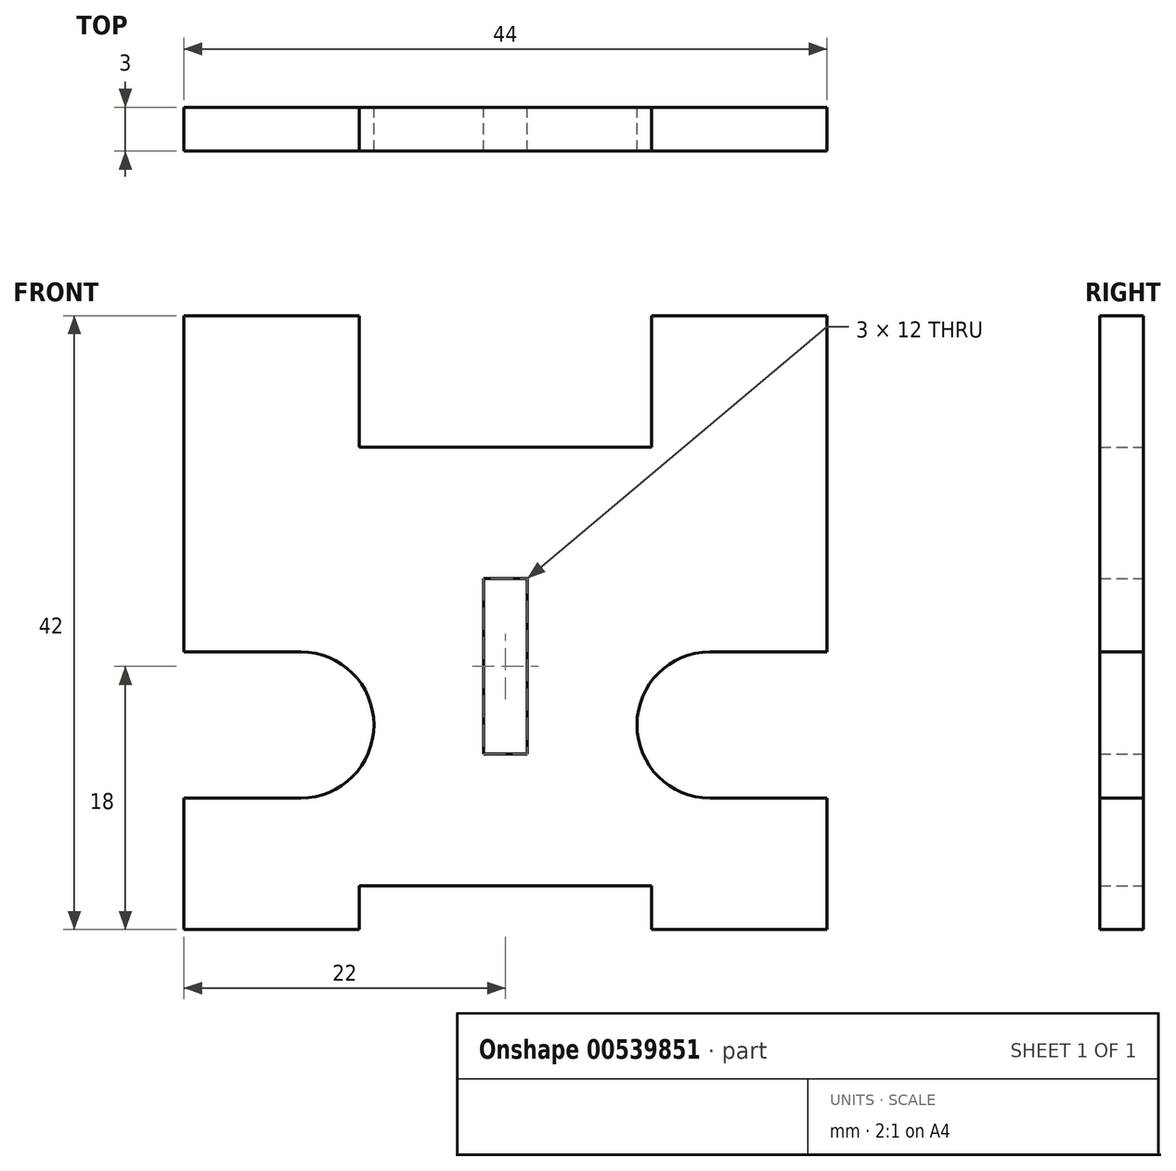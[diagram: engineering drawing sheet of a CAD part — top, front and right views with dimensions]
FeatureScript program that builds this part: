
annotation { "Feature Type Name" : "Feature", "Feature Type Description" : "" }
export const myFeature = defineFeature(function(context is Context, id is Id, definition is map)
    precondition{}
    {
        {
            var Q0;
            Q0=qCreatedBy(makeId("Front.planeOp"),FACE);
            var sketch = newSketch(context, id + "F0", { "sketchPlane" : qUnion([Q0])});
            skLineSegment(sketch, "E0.bottom", {"start": v(10, 15) * mm, "end": v(-10, 15) * mm});
            skLineSegment(sketch, "E0.top", {"start": v(10, -15) * mm, "end": v(-10, -15) * mm});
            skLineSegment(sketch, "E0.left", {"start": v(22, 15) * mm, "end": v(22, 1) * mm});
            skLineSegment(sketch, "E0.right", {"start": v(-22, 15) * mm, "end": v(-22, 1) * mm});
            skPoint(sketch, "E0.middle", {"position": v(0, 0) * mm});
            skLineSegment(sketch, "E1.bottom", {"start": v(1.5, 6) * mm, "end": v(-1.5, 6) * mm});
            skLineSegment(sketch, "E1.top", {"start": v(1.5, -6) * mm, "end": v(-1.5, -6) * mm});
            skLineSegment(sketch, "E1.left", {"start": v(1.5, 6) * mm, "end": v(1.5, -6) * mm});
            skLineSegment(sketch, "E1.right", {"start": v(-1.5, 6) * mm, "end": v(-1.5, -6) * mm});
            skLineSegment(sketch, "E2.top", {"start": v(-22, 24) * mm, "end": v(-10, 24) * mm});
            skLineSegment(sketch, "E2.left", {"start": v(-22, 15) * mm, "end": v(-22, 24) * mm});
            skLineSegment(sketch, "E2.right", {"start": v(-10, 15) * mm, "end": v(-10, 24) * mm});
            skLineSegment(sketch, "E3", {"start": v(0, 0) * mm, "end": v(0, 27.85) * mm, "construction": true});
            skPoint(sketch, "E3.endSnap0", {"position": v(0, 15) * mm});
            skLineSegment(sketch, "E4", {"start": v(0, 0) * mm, "end": v(11.75, 0) * mm, "construction": true});
            skLineSegment(sketch, "E5.MirrorCS", {"start": v(10, 15) * mm, "end": v(10, 24) * mm});
            skLineSegment(sketch, "E6.MirrorCS", {"start": v(22, 15) * mm, "end": v(22, 24) * mm});
            skLineSegment(sketch, "E7.MirrorCS", {"start": v(22, 24) * mm, "end": v(10, 24) * mm});
            skLineSegment(sketch, "E8.top", {"start": v(-22, -18) * mm, "end": v(-10, -18) * mm});
            skLineSegment(sketch, "E8.left", {"start": v(-22, -15) * mm, "end": v(-22, -18) * mm});
            skLineSegment(sketch, "E8.right", {"start": v(-10, -15) * mm, "end": v(-10, -18) * mm});
            skLineSegment(sketch, "E9.MirrorCS", {"start": v(10, -15) * mm, "end": v(10, -18) * mm});
            skLineSegment(sketch, "E10.MirrorCS", {"start": v(22, -18) * mm, "end": v(10, -18) * mm});
            skLineSegment(sketch, "E11.MirrorCS", {"start": v(22, -15) * mm, "end": v(22, -18) * mm});
            skArc(sketch, "E12", {"start": v(-14, -9) * mm, "mid": v(-9, -4) * mm, "end": v(-14, 1) * mm});
            skLineSegment(sketch, "E13", {"start": v(-14, 1) * mm, "end": v(-22, 1) * mm});
            skLineSegment(sketch, "E14", {"start": v(-14, -9) * mm, "end": v(-22, -9) * mm});
            skLineSegment(sketch, "E15.trimOffspring", {"start": v(-22, -9) * mm, "end": v(-22, -15) * mm});
            skArc(sketch, "E16.MirrorCS", {"start": v(14, -9) * mm, "mid": v(9, -4) * mm, "end": v(14, 1) * mm});
            skLineSegment(sketch, "E17.MirrorCS", {"start": v(14, 1) * mm, "end": v(22, 1) * mm});
            skLineSegment(sketch, "E18.MirrorCS", {"start": v(14, -9) * mm, "end": v(22, -9) * mm});
            skLineSegment(sketch, "E19.trimOffspring", {"start": v(22, -9) * mm, "end": v(22, -15) * mm});
            skSolve(sketch);
        }
        {
            var Q0;
            Q0=makeQuery(id+"F0.imprint","IMPRINT",FACE,{"disambiguationData":[TD([[makeQuery(id+"F0.imprint","IMPRINT",EDGE,{"derivedFrom":sQuery(id+"F0.wireOp",EDGE,"E0.bottom")}),1.0]])]});
            extrude(context, id + "F1", {"entities" : qUnion([Q0]), "depth" : 3 * mm, "offsetDistance" : 25 * mm});
        }
    });
